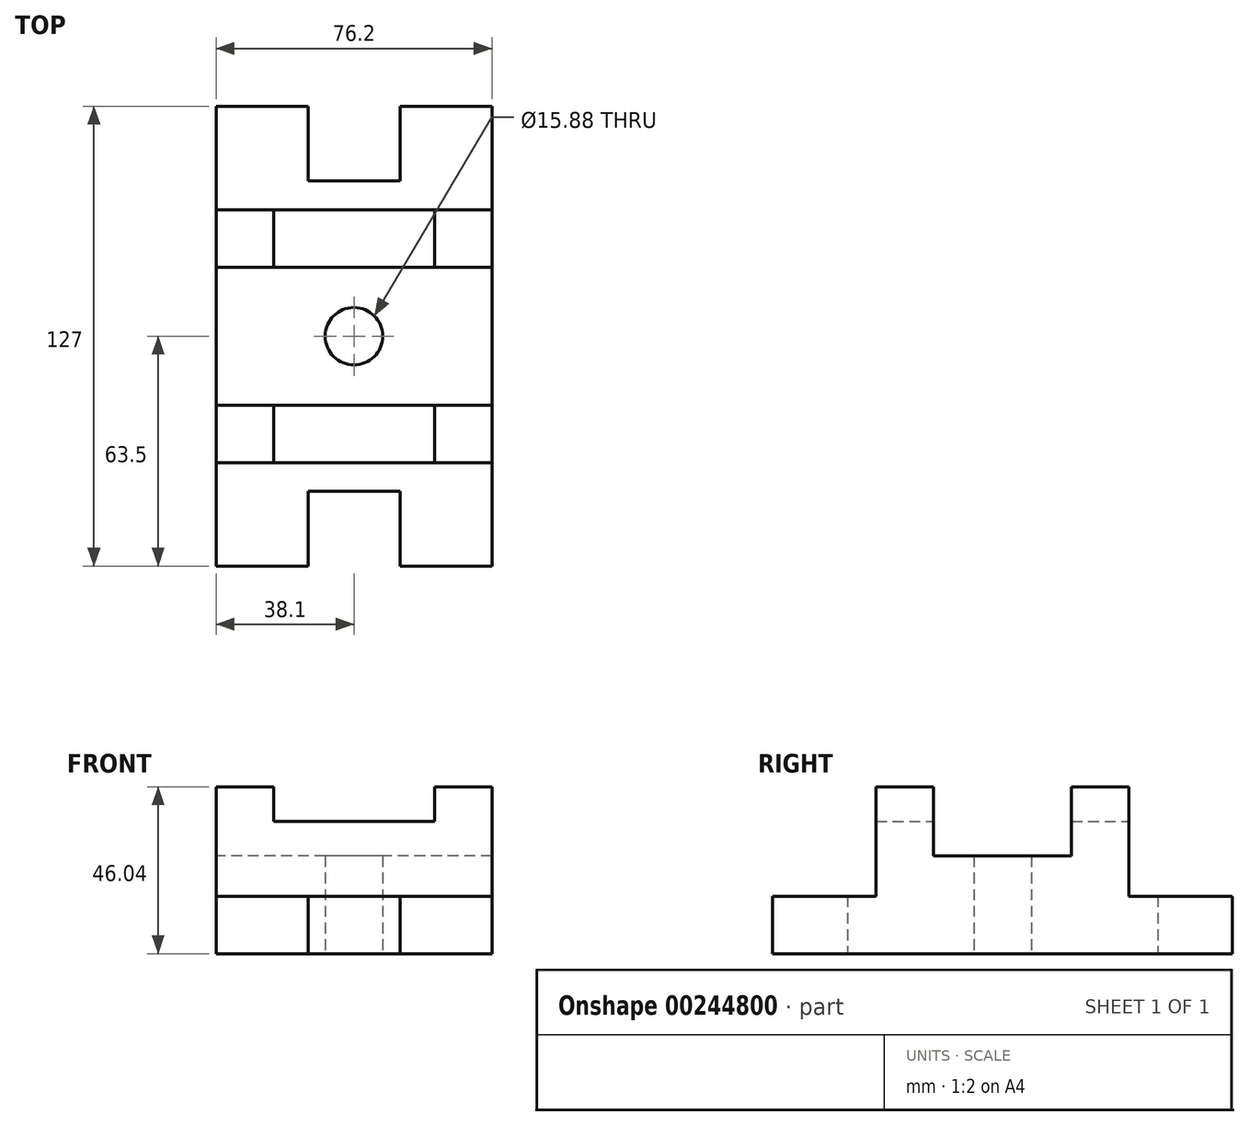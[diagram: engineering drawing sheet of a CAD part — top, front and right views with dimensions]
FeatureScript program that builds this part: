
annotation { "Feature Type Name" : "Feature", "Feature Type Description" : "" }
export const myFeature = defineFeature(function(context is Context, id is Id, definition is map)
    precondition{}
    {
        {
            var Q0;
            Q0=qCreatedBy(makeId("Top.planeOp"),FACE);
            var sketch = newSketch(context, id + "F0", { "sketchPlane" : qUnion([Q0])});
            skLineSegment(sketch, "E0.bottom", {"start": v(38.1, 19.05) * mm, "end": v(-38.1, 19.05) * mm});
            skLineSegment(sketch, "E0.top", {"start": v(38.1, -19.05) * mm, "end": v(-38.1, -19.05) * mm});
            skLineSegment(sketch, "E0.left", {"start": v(38.1, 19.05) * mm, "end": v(38.1, -19.05) * mm});
            skLineSegment(sketch, "E0.right", {"start": v(-38.1, 19.05) * mm, "end": v(-38.1, -19.05) * mm});
            skPoint(sketch, "E0.middle", {"position": v(0, 0) * mm});
            skLineSegment(sketch, "E1", {"start": v(38.1, 19.05) * mm, "end": v(38.1, 34.92) * mm});
            skLineSegment(sketch, "E2", {"start": v(22.22, 19.05) * mm, "end": v(22.22, 34.92) * mm});
            skLineSegment(sketch, "E3", {"start": v(22.22, 34.92) * mm, "end": v(38.1, 34.92) * mm});
            skLineSegment(sketch, "E4", {"start": v(-38.1, 19.05) * mm, "end": v(-38.1, 34.92) * mm});
            skLineSegment(sketch, "E5", {"start": v(-38.1, 34.92) * mm, "end": v(-22.23, 34.92) * mm});
            skLineSegment(sketch, "E6", {"start": v(-22.23, 34.92) * mm, "end": v(-22.23, 19.05) * mm});
            skLineSegment(sketch, "E7", {"start": v(-22.23, 34.92) * mm, "end": v(22.22, 34.92) * mm});
            skLineSegment(sketch, "E8", {"start": v(-38.1, -19.05) * mm, "end": v(-38.1, -34.93) * mm});
            skLineSegment(sketch, "E9", {"start": v(-38.1, -34.93) * mm, "end": v(-22.22, -34.93) * mm});
            skLineSegment(sketch, "E10", {"start": v(-22.23, -34.93) * mm, "end": v(-22.23, -19.05) * mm});
            skLineSegment(sketch, "E11", {"start": v(38.1, -19.05) * mm, "end": v(38.1, -34.92) * mm});
            skLineSegment(sketch, "E12", {"start": v(38.1, -34.92) * mm, "end": v(22.22, -34.92) * mm});
            skLineSegment(sketch, "E13", {"start": v(22.22, -34.92) * mm, "end": v(22.22, -19.05) * mm});
            skLineSegment(sketch, "E14", {"start": v(-22.22, -34.93) * mm, "end": v(22.22, -34.92) * mm});
            skLineSegment(sketch, "E15", {"start": v(38.1, -34.92) * mm, "end": v(38.1, -63.5) * mm});
            skLineSegment(sketch, "E16", {"start": v(38.1, -63.5) * mm, "end": v(12.7, -63.5) * mm});
            skLineSegment(sketch, "E17", {"start": v(12.7, -63.5) * mm, "end": v(12.7, -42.86) * mm});
            skLineSegment(sketch, "E18", {"start": v(12.7, -42.86) * mm, "end": v(-12.7, -42.86) * mm});
            skLineSegment(sketch, "E19", {"start": v(-12.7, -42.86) * mm, "end": v(-12.7, -63.5) * mm});
            skLineSegment(sketch, "E20", {"start": v(-12.7, -63.5) * mm, "end": v(-38.1, -63.5) * mm});
            skLineSegment(sketch, "E21", {"start": v(-38.1, -63.5) * mm, "end": v(-38.1, -34.93) * mm});
            skLineSegment(sketch, "E22", {"start": v(-38.1, 34.92) * mm, "end": v(-38.1, 63.5) * mm});
            skLineSegment(sketch, "E23", {"start": v(38.1, 34.92) * mm, "end": v(38.1, 63.5) * mm});
            skLineSegment(sketch, "E24", {"start": v(38.1, 63.5) * mm, "end": v(12.7, 63.5) * mm});
            skLineSegment(sketch, "E25", {"start": v(12.7, 63.5) * mm, "end": v(12.7, 42.86) * mm});
            skLineSegment(sketch, "E26", {"start": v(12.7, 42.86) * mm, "end": v(-12.7, 42.86) * mm});
            skLineSegment(sketch, "E27", {"start": v(-12.7, 42.86) * mm, "end": v(-12.7, 63.5) * mm});
            skLineSegment(sketch, "E28", {"start": v(-12.7, 63.5) * mm, "end": v(-38.1, 63.5) * mm});
            skCircle(sketch, "E29", {"center": v(0, 0) * mm, "radius": 7.94 * mm});
            skSolve(sketch);
        }
        {
            var Q0;
            Q0 = qSketchRegion(id + "F0", true);
            var Q1;
            {var subQ0=sQuery(id+"F0.wireOp",EDGE,"E2");Q1=makeQuery(id+"F0.imprint","IMPRINT",FACE,{"disambiguationData":[TD([[makeQuery(id+"F0.imprint","IMPRINT",EDGE,{"derivedFrom":subQ0}),1.0]])]});}
            var Q2;
            {var subQ0=sQuery(id+"F0.wireOp",EDGE,"E10");Q2=makeQuery(id+"F0.imprint","IMPRINT",FACE,{"disambiguationData":[TD([[makeQuery(id+"F0.imprint","IMPRINT",EDGE,{"derivedFrom":subQ0}),-1.0]])]});}
            extrude(context, id + "F1", {"entities" : qUnion([Q0, Q1, Q2]), "depth" : 15.88 * mm});
        }
        {
            var Q0;
            {var subQ0=sQuery(id+"F0.wireOp",EDGE,"E2");Q0=makeQuery(id+"F0.imprint","IMPRINT",FACE,{"disambiguationData":[TD([[makeQuery(id+"F0.imprint","IMPRINT",EDGE,{"derivedFrom":subQ0}),1.0]])]});}
            var Q1;
            {var subQ0=sQuery(id+"F0.wireOp",EDGE,"E10");Q1=makeQuery(id+"F0.imprint","IMPRINT",FACE,{"disambiguationData":[TD([[makeQuery(id+"F0.imprint","IMPRINT",EDGE,{"derivedFrom":subQ0}),-1.0]])]});}
            extrude(context, id + "F2", {"entities" : qUnion([Q0, Q1]), "operationType" : NewBodyOperationType.ADD, "depth" : 36.5 * mm});
        }
        {
            var Q0;
            {var subQ0=sQuery(id+"F0.wireOp",EDGE,"E4");Q0=makeQuery(id+"F0.imprint","IMPRINT",FACE,{"disambiguationData":[TD([[makeQuery(id+"F0.imprint","IMPRINT",EDGE,{"derivedFrom":subQ0}),-1.0]])]});}
            var Q1;
            {var subQ0=sQuery(id+"F0.wireOp",EDGE,"E1");Q1=makeQuery(id+"F0.imprint","IMPRINT",FACE,{"disambiguationData":[TD([[makeQuery(id+"F0.imprint","IMPRINT",EDGE,{"derivedFrom":subQ0}),1.0]])]});}
            var Q2;
            {var subQ0=sQuery(id+"F0.wireOp",EDGE,"E8");Q2=makeQuery(id+"F0.imprint","IMPRINT",FACE,{"disambiguationData":[TD([[makeQuery(id+"F0.imprint","IMPRINT",EDGE,{"derivedFrom":subQ0}),1.0]])]});}
            var Q3;
            {var subQ0=sQuery(id+"F0.wireOp",EDGE,"E11");Q3=makeQuery(id+"F0.imprint","IMPRINT",FACE,{"disambiguationData":[TD([[makeQuery(id+"F0.imprint","IMPRINT",EDGE,{"derivedFrom":subQ0}),-1.0]])]});}
            extrude(context, id + "F3", {"entities" : qUnion([Q0, Q1, Q2, Q3]), "operationType" : NewBodyOperationType.ADD, "depth" : 46.04 * mm});
        }
        {
            var Q0;
            {var subQ0=sQuery(id+"F0.wireOp",EDGE,"E0.left");Q0=makeQuery(id+"F0.imprint","IMPRINT",FACE,{"disambiguationData":[TD([[makeQuery(id+"F0.imprint","IMPRINT",EDGE,{"derivedFrom":subQ0}),-1.0]])]});}
            extrude(context, id + "F4", {"entities" : qUnion([Q0]), "operationType" : NewBodyOperationType.ADD, "depth" : 26.99 * mm});
        }
    });
